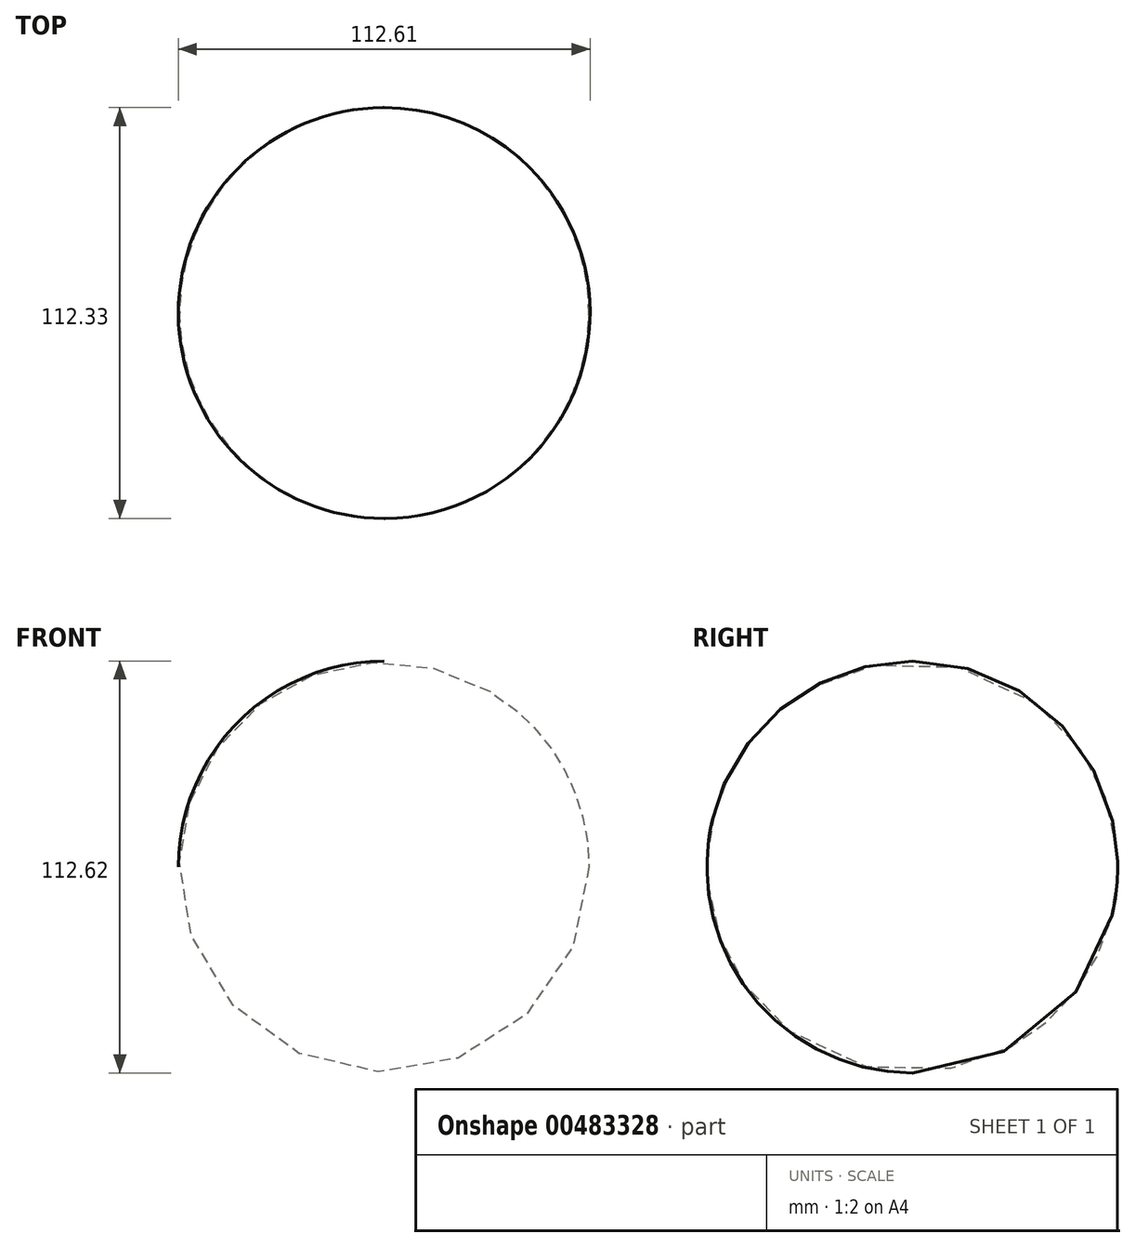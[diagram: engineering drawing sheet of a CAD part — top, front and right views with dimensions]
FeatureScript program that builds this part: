
annotation { "Feature Type Name" : "Feature", "Feature Type Description" : "" }
export const myFeature = defineFeature(function(context is Context, id is Id, definition is map)
    precondition{}
    {
        {
            var Q0;
            Q0=qCreatedBy(makeId("Top.planeOp"),FACE);
            var sketch = newSketch(context, id + "F0", { "sketchPlane" : qUnion([Q0])});
            skArc(sketch, "E0", {"start": v(0.21, 55.74) * mm, "mid": v(-55.66, -0.57) * mm, "end": v(0.5, -56.58) * mm});
            skLineSegment(sketch, "E1", {"start": v(0.21, 55.74) * mm, "end": v(0.5, -56.58) * mm});
            skSolve(sketch);
        }
        {
            var Q0;
            Q0=makeQuery(id+"F0.imprint","IMPRINT",FACE,{"disambiguationData":[TD([[makeQuery(id+"F0.imprint","IMPRINT",EDGE,{"derivedFrom":sQuery(id+"F0.wireOp",EDGE,"E0")}),1.0]])]});
            var Q1;
            Q1=sQuery(id+"F0.wireOp",EDGE,"E1");
            revolve(context, id + "F1", {"entities" : qUnion([Q0]), "axis" : qUnion([Q1]), "revolveType" : RevolveType.FULL});
        }
    });
